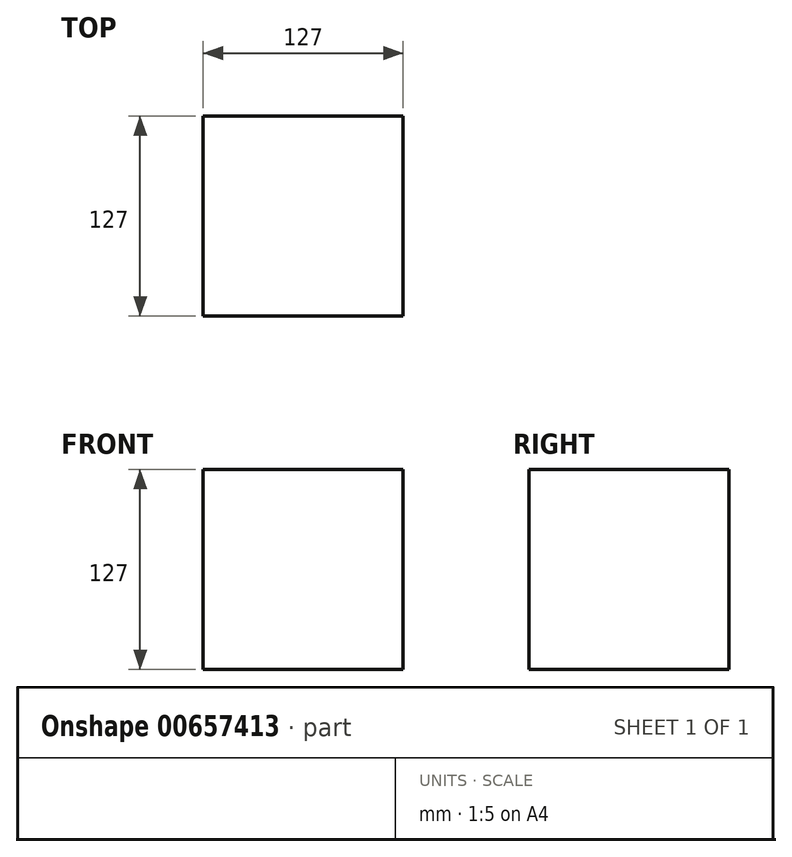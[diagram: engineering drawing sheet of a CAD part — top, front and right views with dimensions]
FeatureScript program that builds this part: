
annotation { "Feature Type Name" : "Feature", "Feature Type Description" : "" }
export const myFeature = defineFeature(function(context is Context, id is Id, definition is map)
    precondition{}
    {
        {
            var Q0;
            Q0=qCreatedBy(makeId("Top.planeOp"),FACE);
            var sketch = newSketch(context, id + "F0", { "sketchPlane" : qUnion([Q0])});
            skLineSegment(sketch, "E0.bottom", {"start": v(0, 0) * mm, "end": v(-127, 0) * mm});
            skLineSegment(sketch, "E0.top", {"start": v(0, 127) * mm, "end": v(-127, 127) * mm});
            skLineSegment(sketch, "E0.left", {"start": v(0, 0) * mm, "end": v(0, 127) * mm});
            skLineSegment(sketch, "E0.right", {"start": v(-127, 0) * mm, "end": v(-127, 127) * mm});
            skSolve(sketch);
        }
        {
            var Q0;
            Q0=makeQuery(id+"F0.imprint","IMPRINT",FACE,{"disambiguationData":[TD([[makeQuery(id+"F0.imprint","IMPRINT",EDGE,{"derivedFrom":sQuery(id+"F0.wireOp",EDGE,"E0.bottom")}),-1.0]])]});
            extrude(context, id + "F1", {"entities" : qUnion([Q0]), "depth" : 127 * mm, "offsetDistance" : 25.4 * mm});
        }
    });
